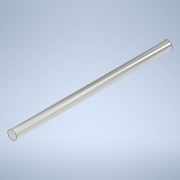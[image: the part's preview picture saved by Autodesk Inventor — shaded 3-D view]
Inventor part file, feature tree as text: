
AUTODESK INVENTOR PART (.ipt)
format: ipt  version: 2022 (Build 260153000, 153)  size: 97,280 bytes
history: native  units: mm
features: extrude x1, sketch x1
ambient origin geometry x8: Origin, YZ Plane, XZ Plane, XY Plane, X Axis, Y Axis, Z Axis, Center Point
bodies: Solid1 (feature_tree)
feature tree (2):
  extrude  "Extrusion1"  Depth=180.0mm TaperAngle=0.0deg
  sketch  "Sketch1"  dims[d0=10.0mm d1=180.0mm d2=0.0mm]
